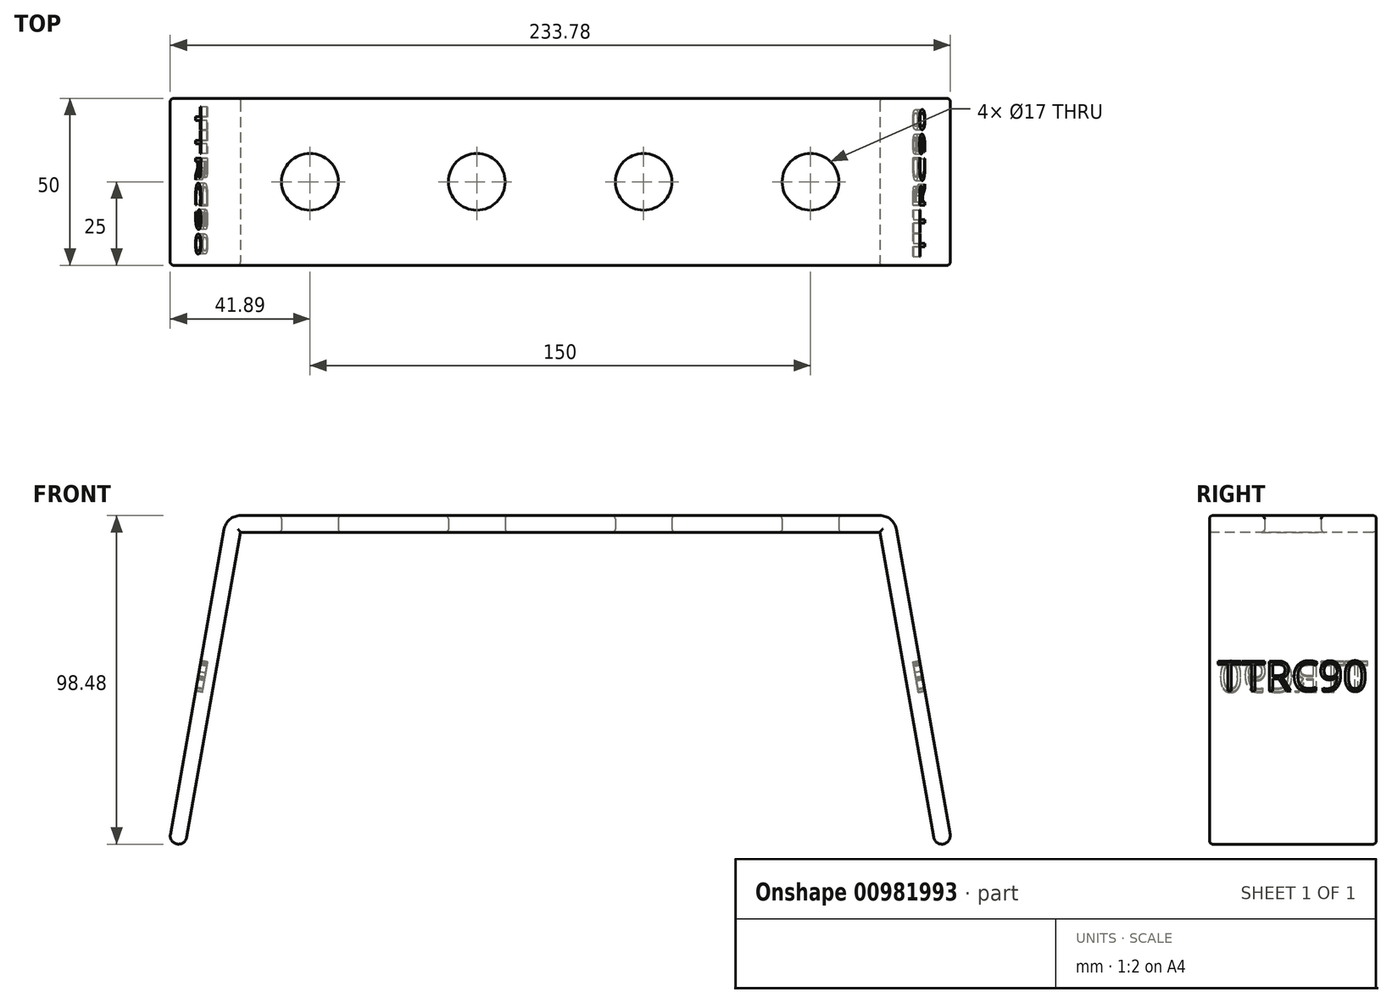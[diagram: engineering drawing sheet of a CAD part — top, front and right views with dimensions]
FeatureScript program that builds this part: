
annotation { "Feature Type Name" : "Feature", "Feature Type Description" : "" }
export const myFeature = defineFeature(function(context is Context, id is Id, definition is map)
    precondition{}
    {
        {
            var Q0;
            Q0=qCreatedBy(makeId("Top.planeOp"),FACE);
            var sketch = newSketch(context, id + "F0", { "sketchPlane" : qUnion([Q0])});
            skLineSegment(sketch, "E0.bottom", {"start": v(100, 25) * mm, "end": v(-100, 25) * mm});
            skLineSegment(sketch, "E0.top", {"start": v(100, -25) * mm, "end": v(-100, -25) * mm});
            skLineSegment(sketch, "E0.left", {"start": v(100, 25) * mm, "end": v(100, -25) * mm});
            skLineSegment(sketch, "E0.right", {"start": v(-100, 25) * mm, "end": v(-100, -25) * mm});
            skPoint(sketch, "E0.middle", {"position": v(0, 0) * mm});
            skLineSegment(sketch, "E1", {"start": v(-100, 0) * mm, "end": v(100, 0) * mm, "construction": true});
            skCircle(sketch, "E2", {"center": v(-75, 0) * mm, "radius": 8.5 * mm});
            skCircle(sketch, "E3", {"center": v(-25, 0) * mm, "radius": 8.5 * mm});
            skCircle(sketch, "E4", {"center": v(25, 0) * mm, "radius": 8.5 * mm});
            skCircle(sketch, "E5", {"center": v(75, 0) * mm, "radius": 8.5 * mm});
            skSolve(sketch);
        }
        {
            var Q0;
            Q0 = qSketchRegion(id + "F0", true);
            extrude(context, id + "F1", {"entities" : qUnion([Q0]), "depth" : 5 * mm, "offsetDistance" : 25 * mm});
        }
        {
            var Q0;
            Q0=makeQuery(id+"F1.opExtrude","SWEPT_FACE",FACE,{"disambiguationData":[OSD([sQuery(id+"F0.wireOp",EDGE,"E0.top")])]});
            var sketch = newSketch(context, id + "F2", { "sketchPlane" : qUnion([Q0])});
            skLineSegment(sketch, "E6", {"start": v(-100, 5) * mm, "end": v(-117.36, -93.48) * mm});
            skLineSegment(sketch, "E7", {"start": v(-117.36, -93.48) * mm, "end": v(-112.29, -93.48) * mm});
            skLineSegment(sketch, "E8", {"start": v(-112.29, -93.48) * mm, "end": v(-95.8, 0) * mm});
            skLineSegment(sketch, "E9", {"start": v(-100, 5) * mm, "end": v(-95.8, 0) * mm});
            skLineSegment(sketch, "E10.MirrorCS", {"start": v(100, 5) * mm, "end": v(95.8, 0) * mm});
            skLineSegment(sketch, "E11.MirrorCS", {"start": v(117.36, -93.48) * mm, "end": v(112.29, -93.48) * mm});
            skLineSegment(sketch, "E12.MirrorCS", {"start": v(100, 5) * mm, "end": v(117.36, -93.48) * mm});
            skLineSegment(sketch, "E13.MirrorCS", {"start": v(112.29, -93.48) * mm, "end": v(95.8, 0) * mm});
            skSolve(sketch);
        }
        {
            var Q0;
            Q0 = qSketchRegion(id + "F2", true);
            extrude(context, id + "F3", {"entities" : qUnion([Q0]), "operationType" : NewBodyOperationType.ADD, "oppositeDirection" : true, "depth" : 50 * mm, "offsetDistance" : 25 * mm});
        }
        {
            var Q0;
            Q0=makeQuery(id+"F3.opExtrude","SWEPT_EDGE",EDGE,{"disambiguationData":[OSD([sQuery(id+"F0.wireOp",EDGE,"E0.top"),sQuery(id+"F2.wireOp",EDGE,"E10.MirrorCS"),sQuery(id+"F2.wireOp",EDGE,"E13.MirrorCS")])]});
            var Q1;
            Q1=makeQuery(id+"F3.opExtrude","SWEPT_EDGE",EDGE,{"disambiguationData":[OSD([sQuery(id+"F0.wireOp",EDGE,"E0.top"),sQuery(id+"F2.wireOp",EDGE,"E8"),sQuery(id+"F2.wireOp",EDGE,"E9")])]});
            var Q2;
            {var subQ0=sQuery(id+"F0.wireOp",EDGE,"E0.right");Q2=makeQuery(id+"F3.boolean.opBoolean","MERGE",EDGE,{"derivedFrom":[makeQuery(id+"F1.opExtrude","CAP_EDGE",EDGE,{"disambiguationData":[OSD([subQ0])],"isStart":false}),makeQuery(id+"F3.opExtrude","SWEPT_EDGE",EDGE,{"disambiguationData":[OSD([sQuery(id+"F0.wireOp",EDGE,"E0.top"),subQ0,sQuery(id+"F2.wireOp",EDGE,"E6"),sQuery(id+"F2.wireOp",EDGE,"E9")])]})]});}
            var Q3;
            {var subQ0=sQuery(id+"F0.wireOp",EDGE,"E0.left");Q3=makeQuery(id+"F3.boolean.opBoolean","MERGE",EDGE,{"derivedFrom":[makeQuery(id+"F1.opExtrude","CAP_EDGE",EDGE,{"disambiguationData":[OSD([subQ0])],"isStart":false}),makeQuery(id+"F3.opExtrude","SWEPT_EDGE",EDGE,{"disambiguationData":[OSD([sQuery(id+"F0.wireOp",EDGE,"E0.top"),subQ0,sQuery(id+"F2.wireOp",EDGE,"E10.MirrorCS"),sQuery(id+"F2.wireOp",EDGE,"E12.MirrorCS")])]})]});}
            fillet(context, id + "F4", {"entities" : qUnion([Q0, Q1, Q2, Q3]), "radius" : 5 * mm, "tangentPropagation" : true, "allowEdgeOverflow" : false});
        }
        {
            var Q0;
            Q0=makeQuery(id+"F3.opExtrude","SWEPT_EDGE",EDGE,{"disambiguationData":[OSD([sQuery(id+"F2.wireOp",EDGE,"E11.MirrorCS"),sQuery(id+"F2.wireOp",EDGE,"E12.MirrorCS")])]});
            var Q1;
            Q1=makeQuery(id+"F3.opExtrude","SWEPT_EDGE",EDGE,{"disambiguationData":[OSD([sQuery(id+"F2.wireOp",EDGE,"E11.MirrorCS"),sQuery(id+"F2.wireOp",EDGE,"E13.MirrorCS")])]});
            var Q2;
            Q2=makeQuery(id+"F3.opExtrude","SWEPT_EDGE",EDGE,{"disambiguationData":[OSD([sQuery(id+"F2.wireOp",EDGE,"E7"),sQuery(id+"F2.wireOp",EDGE,"E8")])]});
            var Q3;
            Q3=makeQuery(id+"F3.opExtrude","SWEPT_EDGE",EDGE,{"disambiguationData":[OSD([sQuery(id+"F2.wireOp",EDGE,"E6"),sQuery(id+"F2.wireOp",EDGE,"E7")])]});
            fillet(context, id + "F5", {"entities" : qUnion([Q0, Q1, Q2, Q3]), "radius" : 2.5 * mm, "tangentPropagation" : true, "allowEdgeOverflow" : false});
        }
        {
            var Q0;
            Q0=makeQuery(id+"F3.opExtrude","SWEPT_FACE",FACE,{"disambiguationData":[OSD([sQuery(id+"F2.wireOp",EDGE,"E6")])]});
            var sketch = newSketch(context, id + "F6", { "sketchPlane" : qUnion([Q0])});
            skText(sketch, "E14", { "text": "TTRC90\n", "fontName": "OpenSans-Regular.ttf"});
            skLineSegment(sketch, "E15", {"start": v(0, -109.46) * mm, "end": v(0, -16.64) * mm, "construction": true});
            const initialGuessF6  = {"E14": [-0.0225, -0.06586, 1, 0, 0.00922]};
            skSetInitialGuess(sketch, initialGuessF6);
            skSolve(sketch);
        }
        {
            var Q0;
            Q0 = qSketchRegion(id + "F6", true);
            extrude(context, id + "F7", {"entities" : qUnion([Q0]), "operationType" : NewBodyOperationType.REMOVE, "oppositeDirection" : true, "depth" : 2 * mm, "offsetDistance" : 25 * mm});
        }
        {
            var Q0;
            Q0=makeQuery(id+"F3.opExtrude","SWEPT_FACE",FACE,{"disambiguationData":[OSD([sQuery(id+"F2.wireOp",EDGE,"E12.MirrorCS")])]});
            var sketch = newSketch(context, id + "F8", { "sketchPlane" : qUnion([Q0])});
            skText(sketch, "E16", { "text": "TTRC90\n", "fontName": "OpenSans-Regular.ttf"});
            skLineSegment(sketch, "E17", {"start": v(0, -109.46) * mm, "end": v(0, -16.64) * mm, "construction": true});
            const initialGuessF8  = {"E16": [-0.0225, -0.06586, 1, 0, 0.00922]};
            skSetInitialGuess(sketch, initialGuessF8);
            skSolve(sketch);
        }
        {
            var Q0;
            Q0 = qSketchRegion(id + "F8", true);
            extrude(context, id + "F9", {"entities" : qUnion([Q0]), "operationType" : NewBodyOperationType.REMOVE, "oppositeDirection" : true, "depth" : 2 * mm, "offsetDistance" : 25 * mm});
        }
        {
            var Q0;
            Q0=makeQuery(id+"F3.boolean.opBoolean","MERGE",FACE,{"derivedFrom":[makeQuery(id+"F1.opExtrude","SWEPT_FACE",FACE,{"disambiguationData":[OSD([sQuery(id+"F0.wireOp",EDGE,"E0.bottom")])]}),makeQuery(id+"F3.opExtrude","CAP_FACE",FACE,{"disambiguationData":[OSD([sQuery(id+"F2.wireOp",EDGE,"E6"),sQuery(id+"F2.wireOp",EDGE,"E7"),sQuery(id+"F2.wireOp",EDGE,"E8"),sQuery(id+"F2.wireOp",EDGE,"E9")])],"isStart":false}),makeQuery(id+"F3.opExtrude","CAP_FACE",FACE,{"disambiguationData":[OSD([sQuery(id+"F2.wireOp",EDGE,"E10.MirrorCS"),sQuery(id+"F2.wireOp",EDGE,"E11.MirrorCS"),sQuery(id+"F2.wireOp",EDGE,"E12.MirrorCS"),sQuery(id+"F2.wireOp",EDGE,"E13.MirrorCS")])],"isStart":false})]});
            var Q1;
            Q1=makeQuery(id+"F3.boolean.opBoolean","MERGE",FACE,{"derivedFrom":[makeQuery(id+"F1.opExtrude","SWEPT_FACE",FACE,{"disambiguationData":[OSD([sQuery(id+"F0.wireOp",EDGE,"E0.top")])]}),makeQuery(id+"F3.opExtrude","CAP_FACE",FACE,{"disambiguationData":[OSD([sQuery(id+"F2.wireOp",EDGE,"E6"),sQuery(id+"F2.wireOp",EDGE,"E7"),sQuery(id+"F2.wireOp",EDGE,"E8"),sQuery(id+"F2.wireOp",EDGE,"E9")])],"isStart":true}),makeQuery(id+"F3.opExtrude","CAP_FACE",FACE,{"disambiguationData":[OSD([sQuery(id+"F2.wireOp",EDGE,"E10.MirrorCS"),sQuery(id+"F2.wireOp",EDGE,"E11.MirrorCS"),sQuery(id+"F2.wireOp",EDGE,"E12.MirrorCS"),sQuery(id+"F2.wireOp",EDGE,"E13.MirrorCS")])],"isStart":true})]});
            fillet(context, id + "F10", {"entities" : qUnion([Q0, Q1]), "radius" : 1 * mm, "tangentPropagation" : true, "allowEdgeOverflow" : false});
        }
        {
            var Q0;
            Q0=makeQuery(id+"F1.opExtrude","CAP_EDGE",EDGE,{"disambiguationData":[OSD([sQuery(id+"F0.wireOp",EDGE,"E5")])],"isStart":false});
            var Q1;
            Q1=makeQuery(id+"F1.opExtrude","CAP_EDGE",EDGE,{"disambiguationData":[OSD([sQuery(id+"F0.wireOp",EDGE,"E4")])],"isStart":false});
            var Q2;
            Q2=makeQuery(id+"F1.opExtrude","CAP_EDGE",EDGE,{"disambiguationData":[OSD([sQuery(id+"F0.wireOp",EDGE,"E3")])],"isStart":false});
            var Q3;
            Q3=makeQuery(id+"F1.opExtrude","CAP_EDGE",EDGE,{"disambiguationData":[OSD([sQuery(id+"F0.wireOp",EDGE,"E2")])],"isStart":false});
            var Q4;
            Q4=makeQuery(id+"F1.opExtrude","CAP_EDGE",EDGE,{"disambiguationData":[OSD([sQuery(id+"F0.wireOp",EDGE,"E5")])],"isStart":true});
            var Q5;
            Q5=makeQuery(id+"F1.opExtrude","CAP_EDGE",EDGE,{"disambiguationData":[OSD([sQuery(id+"F0.wireOp",EDGE,"E4")])],"isStart":true});
            var Q6;
            Q6=makeQuery(id+"F1.opExtrude","CAP_EDGE",EDGE,{"disambiguationData":[OSD([sQuery(id+"F0.wireOp",EDGE,"E3")])],"isStart":true});
            var Q7;
            Q7=makeQuery(id+"F1.opExtrude","CAP_EDGE",EDGE,{"disambiguationData":[OSD([sQuery(id+"F0.wireOp",EDGE,"E2")])],"isStart":true});
            fillet(context, id + "F11", {"entities" : qUnion([Q0, Q1, Q2, Q3, Q4, Q5, Q6, Q7]), "radius" : 1 * mm, "tangentPropagation" : true, "allowEdgeOverflow" : false});
        }
    });
